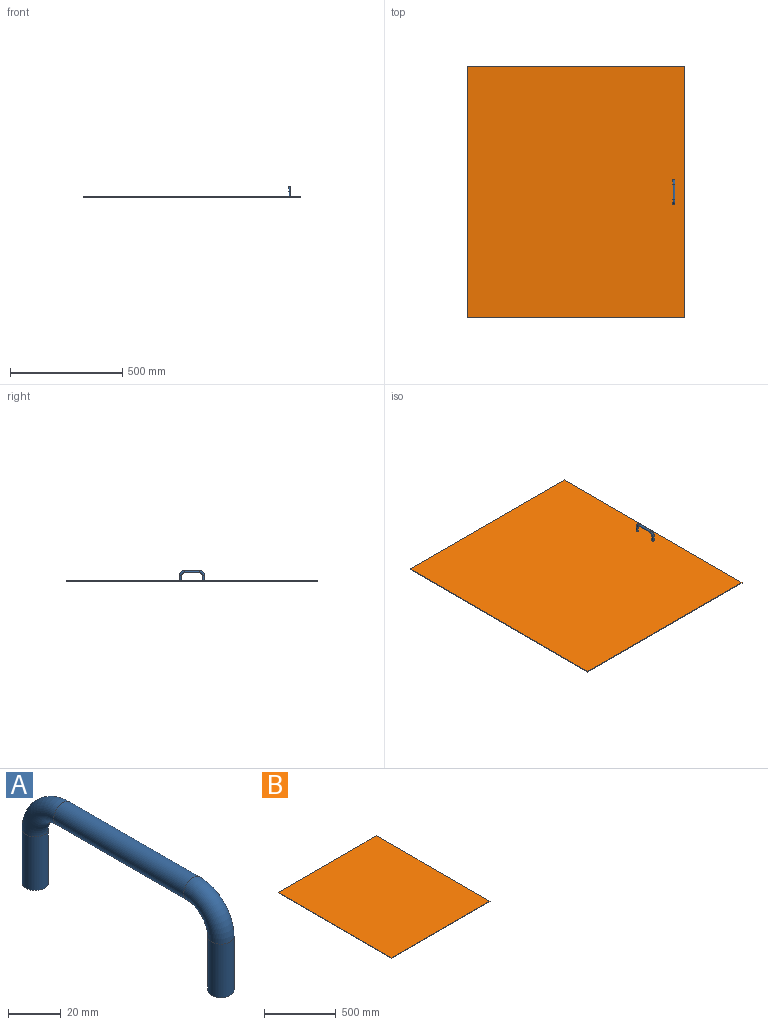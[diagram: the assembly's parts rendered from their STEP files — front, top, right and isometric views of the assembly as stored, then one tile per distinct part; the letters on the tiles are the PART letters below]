
ASSEMBLY  parts=2 mates=1
PART A: 7 faces, bbox 10x113.3x46.6 mm
  f0: plane 10x10mm, normal (0,0,-1), area 78.5mm2, adj f2
  f1: plane 10x10mm, normal (0,0,-1), area 78.5mm2, adj f6
  f2: cylinder r=5mm len=25mm, axis (0,0,1), area 785.4mm2, adj f0,f3
  f3: torus R=15mm, axis (-1,0,0), area 740.2mm2, adj f2,f4
  f4: cylinder r=5mm len=70mm, axis (0,1,0), area 2199.1mm2, adj f3,f5
  f5: torus R=15mm, axis (-1,0,0), area 740.2mm2, adj f4,f6
  f6: cylinder r=5mm len=25mm, axis (0,0,-1), area 785.4mm2, adj f1,f5
PART B: 6 faces, bbox 970x1120x3 mm
  f0: plane 970x3mm, normal (0,1,0), area 2910mm2, adj f1,f3,f4,f5
  f1: plane 1120x3mm, normal (-1,0,0), area 3360mm2, adj f0,f2,f4,f5
  f2: plane 970x3mm, normal (0,-1,0), area 2910mm2, adj f1,f3,f4,f5
  f3: plane 1120x3mm, normal (1,0,0), area 3360mm2, adj f0,f2,f4,f5
  f4: plane 1120x970mm, normal (0,0,1), area 1086400mm2, adj f0,f1,f2,f3
  f5: plane 1120x970mm, normal (0,0,-1), area 1086400mm2, adj f0,f1,f2,f3
PLACE A t=(-5,2.15,87.93)mm
PLACE B t=(-322.45,-6.09,84.93)mm
MATE fastened A.f2 <-> B.f4  axis (0,0,-1) through (-5,-47.85,87.93)mm
